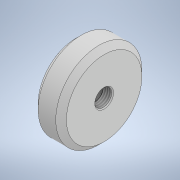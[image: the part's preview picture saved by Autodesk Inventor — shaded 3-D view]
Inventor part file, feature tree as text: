
AUTODESK INVENTOR PART (.ipt)
format: ipt  version: 2022 (Build 260153000, 153)  size: 153,600 bytes
history: native  units: mm
features: sketch x4, revolve x2, hole x2, other x1, thread x1
ambient origin geometry x8: Origin, YZ Plane, XZ Plane, XY Plane, X Axis, Y Axis, Z Axis, Center Point
bodies: Body1 (feature_tree)
feature tree (10):
  other  "Твердое тело1"
  revolve  "Вращение1"
  hole  "Отверстие1"  [1 undecoded]
  revolve  "Вращение2"
  hole  "Отверстие2"  [1 undecoded]
  thread  "Резьба1"
  sketch  "Эскиз1"
  sketch  "Эскиз2"
  sketch  "Эскиз3"
  sketch  "Эскиз4"
note: 2 required parameter values undecoded (feature->parameter linkage not recoverable at this tier; creation-order binding heuristic only, values carry confidence <= 0.55)
